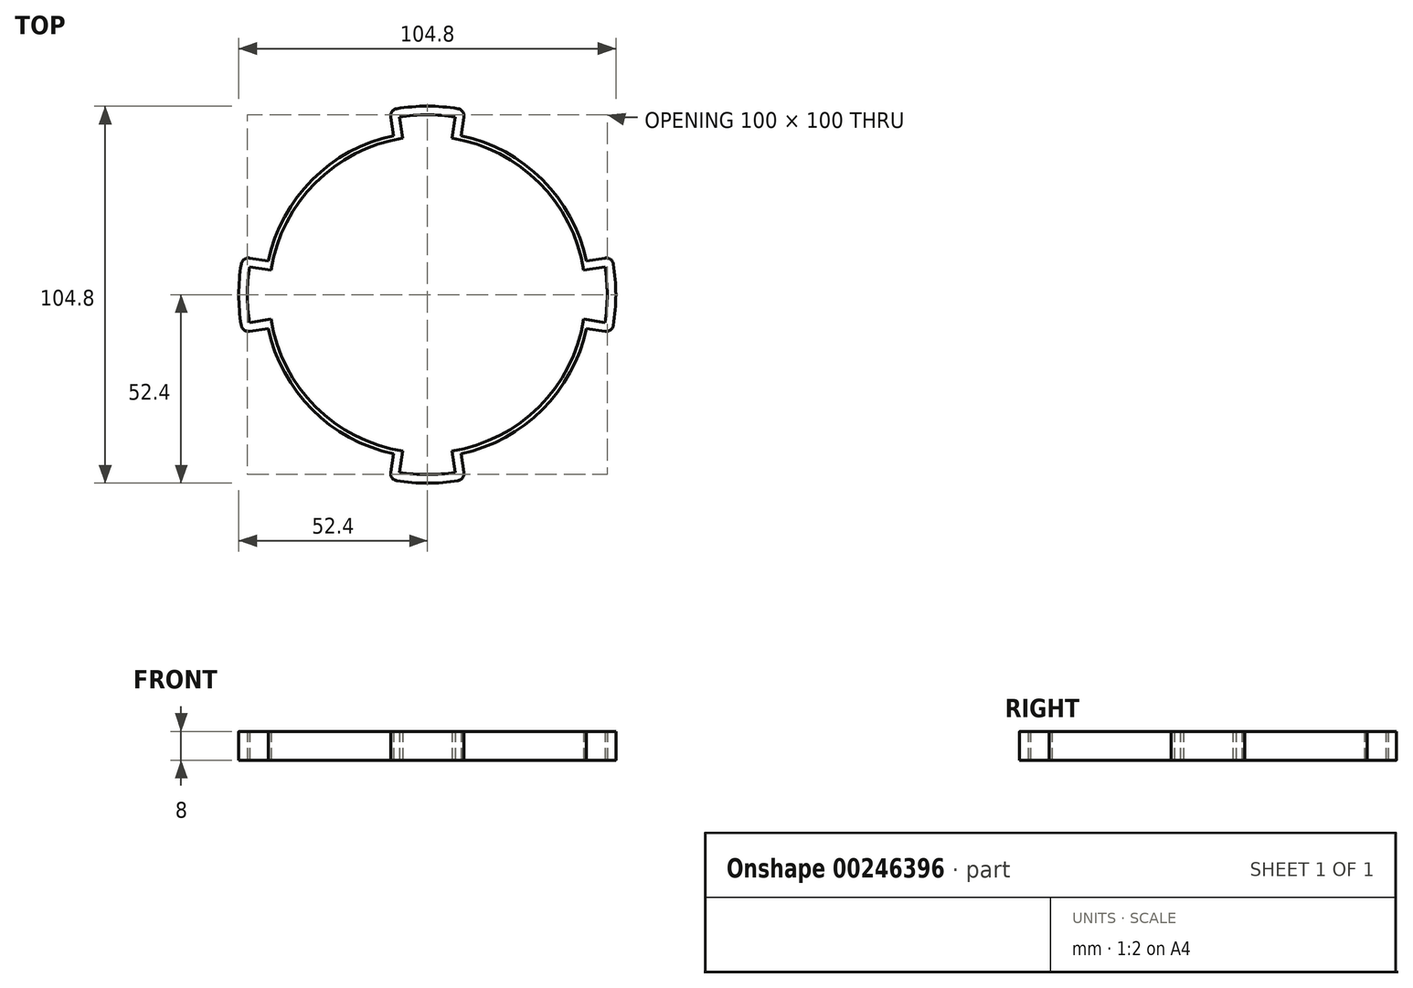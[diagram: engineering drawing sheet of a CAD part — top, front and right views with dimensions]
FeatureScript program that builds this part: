
annotation { "Feature Type Name" : "Feature", "Feature Type Description" : "" }
export const myFeature = defineFeature(function(context is Context, id is Id, definition is map)
    precondition{}
    {
        {
            var Q0;
            Q0=qCreatedBy(makeId("Top.planeOp"),FACE);
            var sketch = newSketch(context, id + "F0", { "sketchPlane" : qUnion([Q0])});
            skCircle(sketch, "E0", {"center": v(0, 0) * mm, "radius": 50 * mm});
            skCircle(sketch, "E1", {"center": v(0, 0) * mm, "radius": 44 * mm});
            skCircle(sketch, "E2", {"center": v(0, 0) * mm, "radius": 45.2 * mm});
            skLineSegment(sketch, "E3", {"start": v(0, 0) * mm, "end": v(0, 50) * mm, "construction": true});
            skLineSegment(sketch, "E4", {"start": v(0, 0) * mm, "end": v(50, 0) * mm, "construction": true});
            skLineSegment(sketch, "E5.MirrorCS", {"start": v(0, 0) * mm, "end": v(-50, 0) * mm, "construction": true});
            skLineSegment(sketch, "E6.MirrorCS", {"start": v(0, 0) * mm, "end": v(0, -50) * mm, "construction": true});
            skLineSegment(sketch, "E7", {"start": v(-7.75, 49.4) * mm, "end": v(0, 49.4) * mm, "construction": true});
            skCircle(sketch, "E8", {"center": v(0, 0) * mm, "radius": 52.4 * mm});
            skLineSegment(sketch, "E9", {"start": v(-9.37, 44.22) * mm, "end": v(-10.48, 51.34) * mm});
            skLineSegment(sketch, "E10.MirrorCS", {"start": v(9.37, 44.22) * mm, "end": v(10.48, 51.34) * mm});
            skLineSegment(sketch, "E11", {"start": v(0, 0) * mm, "end": v(-6.82, 43.47) * mm, "construction": true});
            skLineSegment(sketch, "E12", {"start": v(-6.82, 43.47) * mm, "end": v(-7.75, 49.4) * mm});
            skLineSegment(sketch, "E13.MirrorCS", {"start": v(6.82, 43.47) * mm, "end": v(7.75, 49.4) * mm});
            skLineSegment(sketch, "E14.1.0", {"start": v(-44.22, 9.37) * mm, "end": v(-51.34, 10.48) * mm});
            skLineSegment(sketch, "E14.1.1", {"start": v(-43.47, 6.82) * mm, "end": v(-49.4, 7.75) * mm});
            skLineSegment(sketch, "E14.1.2", {"start": v(-43.47, -6.82) * mm, "end": v(-49.4, -7.75) * mm});
            skLineSegment(sketch, "E14.1.3", {"start": v(-44.22, -9.37) * mm, "end": v(-51.34, -10.48) * mm});
            skLineSegment(sketch, "E14.2.0", {"start": v(-9.37, -44.22) * mm, "end": v(-10.48, -51.34) * mm});
            skLineSegment(sketch, "E14.2.1", {"start": v(-6.82, -43.47) * mm, "end": v(-7.75, -49.4) * mm});
            skLineSegment(sketch, "E14.2.2", {"start": v(6.82, -43.47) * mm, "end": v(7.75, -49.4) * mm});
            skLineSegment(sketch, "E14.2.3", {"start": v(9.37, -44.22) * mm, "end": v(10.48, -51.34) * mm});
            skLineSegment(sketch, "E14.3.0", {"start": v(44.22, -9.37) * mm, "end": v(51.34, -10.48) * mm});
            skLineSegment(sketch, "E14.3.1", {"start": v(43.47, -6.82) * mm, "end": v(49.4, -7.75) * mm});
            skLineSegment(sketch, "E14.3.2", {"start": v(43.47, 6.82) * mm, "end": v(49.4, 7.75) * mm});
            skLineSegment(sketch, "E14.3.3", {"start": v(44.22, 9.37) * mm, "end": v(51.34, 10.48) * mm});
            skSolve(sketch);
        }
        {
            var Q0;
            {var subQ5=sQuery(id+"F0.wireOp",EDGE,"E0");var subQ7=makeQuery(id+"F0.imprint","INTERSECT",VERTEX,{"derivedFrom":[subQ5,sQuery(id+"F0.wireOp",EDGE,"E14.3.2")]});Q0=makeQuery(id+"F0.imprint","IMPRINT",FACE,{"disambiguationData":[TD([[makeQuery(id+"F0.imprint","IMPRINT",EDGE,{"disambiguationData":[TD([[subQ7,-1.0]])],"derivedFrom":subQ5}),-1.0]])]});}
            var Q1;
            {var subQ5=sQuery(id+"F0.wireOp",EDGE,"E0");var subQ7=makeQuery(id+"F0.imprint","INTERSECT",VERTEX,{"derivedFrom":[subQ5,sQuery(id+"F0.wireOp",EDGE,"E13.MirrorCS")]});Q1=makeQuery(id+"F0.imprint","IMPRINT",FACE,{"disambiguationData":[TD([[makeQuery(id+"F0.imprint","IMPRINT",EDGE,{"disambiguationData":[TD([[subQ7,1.0]])],"derivedFrom":subQ5}),-1.0]])]});}
            var Q2;
            {var subQ5=sQuery(id+"F0.wireOp",EDGE,"E0");var subQ8=makeQuery(id+"F0.imprint","INTERSECT",VERTEX,{"derivedFrom":[subQ5,sQuery(id+"F0.wireOp",EDGE,"E14.1.1")]});Q2=makeQuery(id+"F0.imprint","IMPRINT",FACE,{"disambiguationData":[TD([[makeQuery(id+"F0.imprint","IMPRINT",EDGE,{"disambiguationData":[TD([[subQ8,1.0]])],"derivedFrom":subQ5}),-1.0]])]});}
            var Q3;
            {var subQ5=sQuery(id+"F0.wireOp",EDGE,"E0");var subQ8=makeQuery(id+"F0.imprint","INTERSECT",VERTEX,{"derivedFrom":[subQ5,sQuery(id+"F0.wireOp",EDGE,"E14.2.1")]});Q3=makeQuery(id+"F0.imprint","IMPRINT",FACE,{"disambiguationData":[TD([[makeQuery(id+"F0.imprint","IMPRINT",EDGE,{"disambiguationData":[TD([[subQ8,1.0]])],"derivedFrom":subQ5}),-1.0]])]});}
            var Q4;
            {var subQ0=sQuery(id+"F0.wireOp",EDGE,"E12");var subQ1=sQuery(id+"F0.wireOp",EDGE,"E0");var subQ2=makeQuery(id+"F0.imprint","INTERSECT",VERTEX,{"derivedFrom":[subQ1,subQ0]});Q4=makeQuery(id+"F0.imprint","IMPRINT",FACE,{"disambiguationData":[TD([[makeQuery(id+"F0.imprint","IMPRINT",EDGE,{"disambiguationData":[TD([[subQ2,-1.0]])],"derivedFrom":subQ1}),1.0]])]});}
            var Q5;
            {var subQ5=sQuery(id+"F0.wireOp",EDGE,"E12");var subQ7=sQuery(id+"F0.wireOp",EDGE,"E1");var subQ8=makeQuery(id+"F0.imprint","INTERSECT",VERTEX,{"derivedFrom":[subQ7,subQ5]});Q5=makeQuery(id+"F0.imprint","IMPRINT",FACE,{"disambiguationData":[TD([[makeQuery(id+"F0.imprint","IMPRINT",EDGE,{"disambiguationData":[TD([[subQ8,-1.0]])],"derivedFrom":subQ7}),-1.0]])]});}
            var Q6;
            {var subQ0=sQuery(id+"F0.wireOp",EDGE,"E13.MirrorCS");var subQ1=sQuery(id+"F0.wireOp",EDGE,"E0");var subQ2=makeQuery(id+"F0.imprint","INTERSECT",VERTEX,{"derivedFrom":[subQ1,subQ0]});Q6=makeQuery(id+"F0.imprint","IMPRINT",FACE,{"disambiguationData":[TD([[makeQuery(id+"F0.imprint","IMPRINT",EDGE,{"disambiguationData":[TD([[subQ2,1.0]])],"derivedFrom":subQ1}),1.0]])]});}
            var Q7;
            {var subQ2=sQuery(id+"F0.wireOp",EDGE,"E13.MirrorCS");var subQ7=sQuery(id+"F0.wireOp",EDGE,"E1");var subQ8=makeQuery(id+"F0.imprint","INTERSECT",VERTEX,{"derivedFrom":[subQ7,subQ2]});Q7=makeQuery(id+"F0.imprint","IMPRINT",FACE,{"disambiguationData":[TD([[makeQuery(id+"F0.imprint","IMPRINT",EDGE,{"disambiguationData":[TD([[subQ8,1.0]])],"derivedFrom":subQ7}),-1.0]])]});}
            var Q8;
            {var subQ0=sQuery(id+"F0.wireOp",EDGE,"E14.3.2");var subQ1=sQuery(id+"F0.wireOp",EDGE,"E0");var subQ2=makeQuery(id+"F0.imprint","INTERSECT",VERTEX,{"derivedFrom":[subQ1,subQ0]});Q8=makeQuery(id+"F0.imprint","IMPRINT",FACE,{"disambiguationData":[TD([[makeQuery(id+"F0.imprint","IMPRINT",EDGE,{"disambiguationData":[TD([[subQ2,-1.0]])],"derivedFrom":subQ1}),1.0]])]});}
            var Q9;
            {var subQ0=sQuery(id+"F0.wireOp",EDGE,"E14.3.1");var subQ1=sQuery(id+"F0.wireOp",EDGE,"E0");var subQ2=makeQuery(id+"F0.imprint","INTERSECT",VERTEX,{"derivedFrom":[subQ1,subQ0]});Q9=makeQuery(id+"F0.imprint","IMPRINT",FACE,{"disambiguationData":[TD([[makeQuery(id+"F0.imprint","IMPRINT",EDGE,{"disambiguationData":[TD([[subQ2,1.0]])],"derivedFrom":subQ1}),1.0]])]});}
            var Q10;
            {var subQ0=sQuery(id+"F0.wireOp",EDGE,"E14.1.1");var subQ1=sQuery(id+"F0.wireOp",EDGE,"E0");var subQ2=makeQuery(id+"F0.imprint","INTERSECT",VERTEX,{"derivedFrom":[subQ1,subQ0]});Q10=makeQuery(id+"F0.imprint","IMPRINT",FACE,{"disambiguationData":[TD([[makeQuery(id+"F0.imprint","IMPRINT",EDGE,{"disambiguationData":[TD([[subQ2,1.0]])],"derivedFrom":subQ1}),1.0]])]});}
            var Q11;
            {var subQ3=sQuery(id+"F0.wireOp",EDGE,"E14.1.2");var subQ4=sQuery(id+"F0.wireOp",EDGE,"E1");var subQ5=makeQuery(id+"F0.imprint","INTERSECT",VERTEX,{"derivedFrom":[subQ4,subQ3]});Q11=makeQuery(id+"F0.imprint","IMPRINT",FACE,{"disambiguationData":[TD([[makeQuery(id+"F0.imprint","IMPRINT",EDGE,{"disambiguationData":[TD([[subQ5,-1.0]])],"derivedFrom":subQ4}),-1.0]])]});}
            var Q12;
            {var subQ0=sQuery(id+"F0.wireOp",EDGE,"E14.1.2");var subQ1=sQuery(id+"F0.wireOp",EDGE,"E0");var subQ2=makeQuery(id+"F0.imprint","INTERSECT",VERTEX,{"derivedFrom":[subQ1,subQ0]});Q12=makeQuery(id+"F0.imprint","IMPRINT",FACE,{"disambiguationData":[TD([[makeQuery(id+"F0.imprint","IMPRINT",EDGE,{"disambiguationData":[TD([[subQ2,-1.0]])],"derivedFrom":subQ1}),1.0]])]});}
            var Q13;
            {var subQ5=sQuery(id+"F0.wireOp",EDGE,"E14.2.2");var subQ7=sQuery(id+"F0.wireOp",EDGE,"E1");var subQ8=makeQuery(id+"F0.imprint","INTERSECT",VERTEX,{"derivedFrom":[subQ7,subQ5]});Q13=makeQuery(id+"F0.imprint","IMPRINT",FACE,{"disambiguationData":[TD([[makeQuery(id+"F0.imprint","IMPRINT",EDGE,{"disambiguationData":[TD([[subQ8,-1.0]])],"derivedFrom":subQ7}),-1.0]])]});}
            var Q14;
            {var subQ0=sQuery(id+"F0.wireOp",EDGE,"E14.2.2");var subQ1=sQuery(id+"F0.wireOp",EDGE,"E0");var subQ2=makeQuery(id+"F0.imprint","INTERSECT",VERTEX,{"derivedFrom":[subQ1,subQ0]});Q14=makeQuery(id+"F0.imprint","IMPRINT",FACE,{"disambiguationData":[TD([[makeQuery(id+"F0.imprint","IMPRINT",EDGE,{"disambiguationData":[TD([[subQ2,-1.0]])],"derivedFrom":subQ1}),1.0]])]});}
            var Q15;
            {var subQ0=sQuery(id+"F0.wireOp",EDGE,"E14.2.1");var subQ1=sQuery(id+"F0.wireOp",EDGE,"E0");var subQ2=makeQuery(id+"F0.imprint","INTERSECT",VERTEX,{"derivedFrom":[subQ1,subQ0]});Q15=makeQuery(id+"F0.imprint","IMPRINT",FACE,{"disambiguationData":[TD([[makeQuery(id+"F0.imprint","IMPRINT",EDGE,{"disambiguationData":[TD([[subQ2,1.0]])],"derivedFrom":subQ1}),1.0]])]});}
            extrude(context, id + "F1", {"entities" : qUnion([Q0, Q1, Q2, Q3, Q4, Q5, Q6, Q7, Q8, Q9, Q10, Q11, Q12, Q13, Q14, Q15]), "depth" : 8 * mm});
        }
        {
            var Q0;
            Q0=makeQuery(id+"F1.opExtrude","SWEPT_EDGE",EDGE,{"disambiguationData":[OSD([sQuery(id+"F0.wireOp",EDGE,"E8"),sQuery(id+"F0.wireOp",EDGE,"E14.1.3")])]});
            var Q1;
            Q1=makeQuery(id+"F1.opExtrude","SWEPT_EDGE",EDGE,{"disambiguationData":[OSD([sQuery(id+"F0.wireOp",EDGE,"E8"),sQuery(id+"F0.wireOp",EDGE,"E14.1.0")])]});
            var Q2;
            Q2=makeQuery(id+"F1.opExtrude","SWEPT_EDGE",EDGE,{"disambiguationData":[OSD([sQuery(id+"F0.wireOp",EDGE,"E8"),sQuery(id+"F0.wireOp",EDGE,"E9")])]});
            var Q3;
            Q3=makeQuery(id+"F1.opExtrude","SWEPT_EDGE",EDGE,{"disambiguationData":[OSD([sQuery(id+"F0.wireOp",EDGE,"E8"),sQuery(id+"F0.wireOp",EDGE,"E10.MirrorCS")])]});
            var Q4;
            Q4=makeQuery(id+"F1.opExtrude","SWEPT_EDGE",EDGE,{"disambiguationData":[OSD([sQuery(id+"F0.wireOp",EDGE,"E8"),sQuery(id+"F0.wireOp",EDGE,"E14.3.0")])]});
            var Q5;
            Q5=makeQuery(id+"F1.opExtrude","SWEPT_EDGE",EDGE,{"disambiguationData":[OSD([sQuery(id+"F0.wireOp",EDGE,"E8"),sQuery(id+"F0.wireOp",EDGE,"E14.3.3")])]});
            var Q6;
            Q6=makeQuery(id+"F1.opExtrude","SWEPT_EDGE",EDGE,{"disambiguationData":[OSD([sQuery(id+"F0.wireOp",EDGE,"E8"),sQuery(id+"F0.wireOp",EDGE,"E14.2.3")])]});
            var Q7;
            Q7=makeQuery(id+"F1.opExtrude","SWEPT_EDGE",EDGE,{"disambiguationData":[OSD([sQuery(id+"F0.wireOp",EDGE,"E8"),sQuery(id+"F0.wireOp",EDGE,"E14.2.0")])]});
            fillet(context, id + "F2", {"entities" : qUnion([Q0, Q1, Q2, Q3, Q4, Q5, Q6, Q7]), "radius" : 2 * mm, "tangentPropagation" : true, "allowEdgeOverflow" : false});
        }
    });
